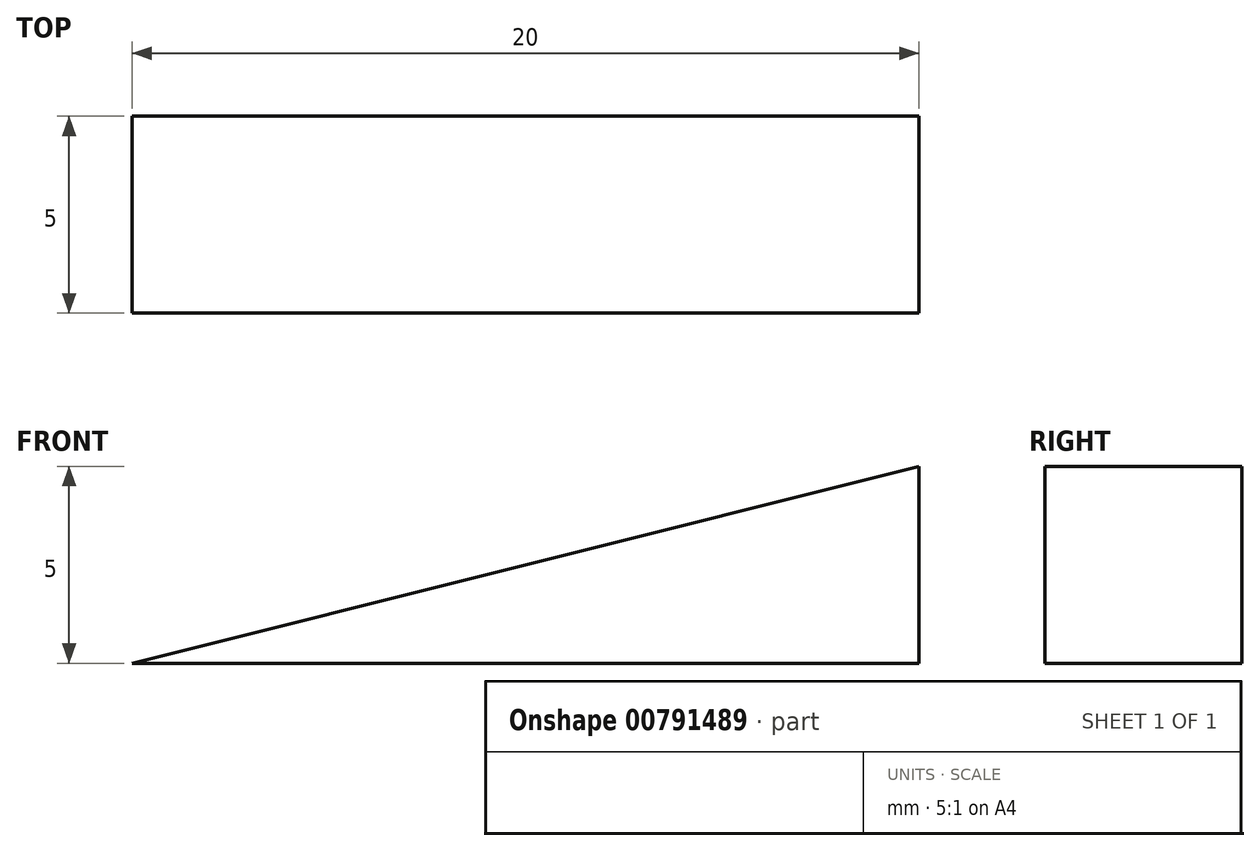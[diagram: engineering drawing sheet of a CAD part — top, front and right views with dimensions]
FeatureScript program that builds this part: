
annotation { "Feature Type Name" : "Feature", "Feature Type Description" : "" }
export const myFeature = defineFeature(function(context is Context, id is Id, definition is map)
    precondition{}
    {
        {
            var Q0;
            Q0=qCreatedBy(makeId("Top.planeOp"),FACE);
            var sketch = newSketch(context, id + "F0", { "sketchPlane" : qUnion([Q0])});
            skLineSegment(sketch, "E0.bottom", {"start": v(10, -2.5) * mm, "end": v(-10, -2.5) * mm});
            skLineSegment(sketch, "E0.top", {"start": v(10, 2.5) * mm, "end": v(-10, 2.5) * mm});
            skLineSegment(sketch, "E0.left", {"start": v(10, -2.5) * mm, "end": v(10, 2.5) * mm});
            skLineSegment(sketch, "E0.right", {"start": v(-10, -2.5) * mm, "end": v(-10, 2.5) * mm});
            skPoint(sketch, "E0.middle", {"position": v(0, 0) * mm});
            skSolve(sketch);
        }
        {
            var Q0;
            Q0=makeQuery(id+"F0.imprint","IMPRINT",FACE,{"disambiguationData":[TD([[makeQuery(id+"F0.imprint","IMPRINT",EDGE,{"derivedFrom":sQuery(id+"F0.wireOp",EDGE,"E0.bottom")}),-1.0]])]});
            extrude(context, id + "F1", {"entities" : qUnion([Q0]), "depth" : 5 * mm, "offsetDistance" : 25 * mm});
        }
        {
            var Q0;
            Q0=makeQuery(id+"F1.opExtrude","SWEPT_FACE",FACE,{"disambiguationData":[OSD([sQuery(id+"F0.wireOp",EDGE,"E0.bottom")])]});
            var sketch = newSketch(context, id + "F2", { "sketchPlane" : qUnion([Q0])});
            skLineSegment(sketch, "E1", {"start": v(-10, 0) * mm, "end": v(10, 5) * mm});
            skSolve(sketch);
        }
        {
            var Q0;
            Q0=makeQuery(id+"F2.imprint","IMPRINT",FACE,{"disambiguationData":[TD([[makeQuery(id+"F2.imprint","IMPRINT",EDGE,{"derivedFrom":sQuery(id+"F2.wireOp",EDGE,"E1")}),1.0]])]});
            extrude(context, id + "F3", {"entities" : qUnion([Q0]), "operationType" : NewBodyOperationType.REMOVE, "oppositeDirection" : true, "depth" : 25 * mm, "offsetDistance" : 25 * mm});
        }
    });
